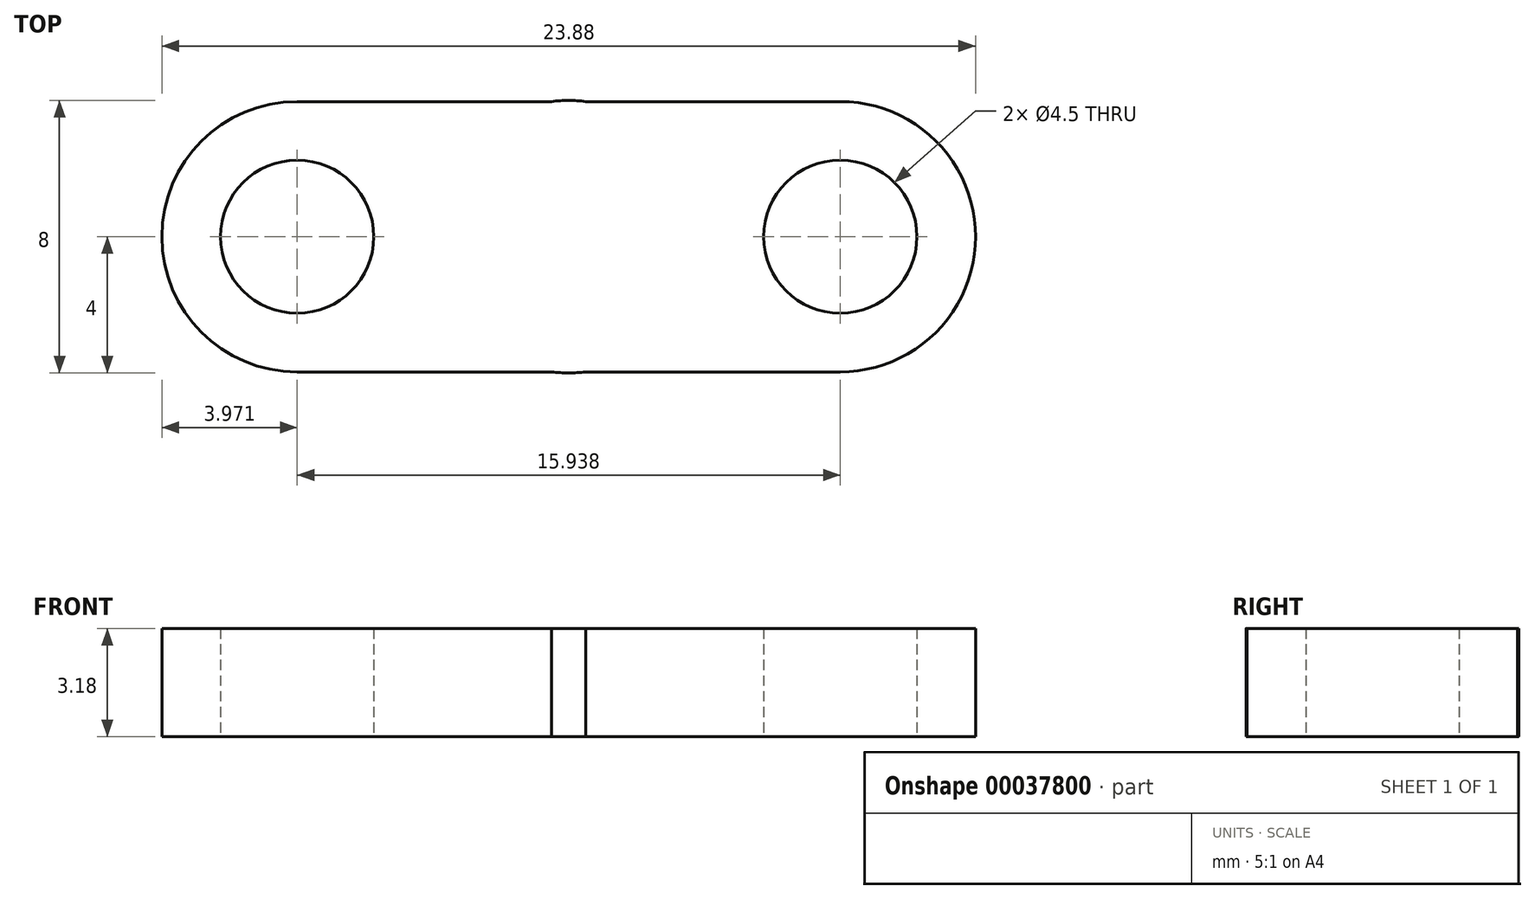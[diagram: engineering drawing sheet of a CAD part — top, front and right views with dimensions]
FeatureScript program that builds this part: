
annotation { "Feature Type Name" : "Feature", "Feature Type Description" : "" }
export const myFeature = defineFeature(function(context is Context, id is Id, definition is map)
    precondition{}
    {
        {
            var Q0;
            Q0=qCreatedBy(makeId("Top.planeOp"),FACE);
            var sketch = newSketch(context, id + "F0", { "sketchPlane" : qUnion([Q0])});
            skArc(sketch, "E0", {"start": v(0.5, 3.97) * mm, "mid": v(0, 4) * mm, "end": v(-0.5, 3.97) * mm});
            skArc(sketch, "E1", {"start": v(7.97, 3.97) * mm, "mid": v(4, 0) * mm, "end": v(7.97, -3.97) * mm, "construction": true});
            skLineSegment(sketch, "E2", {"start": v(-7.97, 0) * mm, "end": v(7.97, 0) * mm, "construction": true});
            skLineSegment(sketch, "E3", {"start": v(7.97, -3.97) * mm, "end": v(7.97, 3.97) * mm, "construction": true});
            skLineSegment(sketch, "E4", {"start": v(-7.97, -3.97) * mm, "end": v(-7.97, 3.97) * mm, "construction": true});
            skLineSegment(sketch, "E5", {"start": v(-7.97, 3.97) * mm, "end": v(-0.5, 3.97) * mm});
            skLineSegment(sketch, "E6", {"start": v(7.97, 3.97) * mm, "end": v(0.5, 3.97) * mm});
            skLineSegment(sketch, "E7", {"start": v(7.97, -3.97) * mm, "end": v(0.5, -3.97) * mm});
            skLineSegment(sketch, "E8", {"start": v(-7.97, -3.97) * mm, "end": v(-0.5, -3.97) * mm});
            skArc(sketch, "E9", {"start": v(-0.5, -3.97) * mm, "mid": v(0, -4) * mm, "end": v(0.5, -3.97) * mm});
            skArc(sketch, "E10", {"start": v(7.97, -3.97) * mm, "mid": v(11.94, 0) * mm, "end": v(7.97, 3.97) * mm});
            skArc(sketch, "E11", {"start": v(-7.97, 3.97) * mm, "mid": v(-11.94, 0) * mm, "end": v(-7.97, -3.97) * mm});
            skCircle(sketch, "E12", {"center": v(-7.97, 0) * mm, "radius": 2.25 * mm});
            skCircle(sketch, "E13", {"center": v(7.97, 0) * mm, "radius": 2.25 * mm});
            skSolve(sketch);
        }
        {
            var Q0;
            Q0 = qSketchRegion(id + "F0", true);
            extrude(context, id + "F1", {"entities" : qUnion([Q0]), "depth" : 3.17 * mm});
        }
    });
